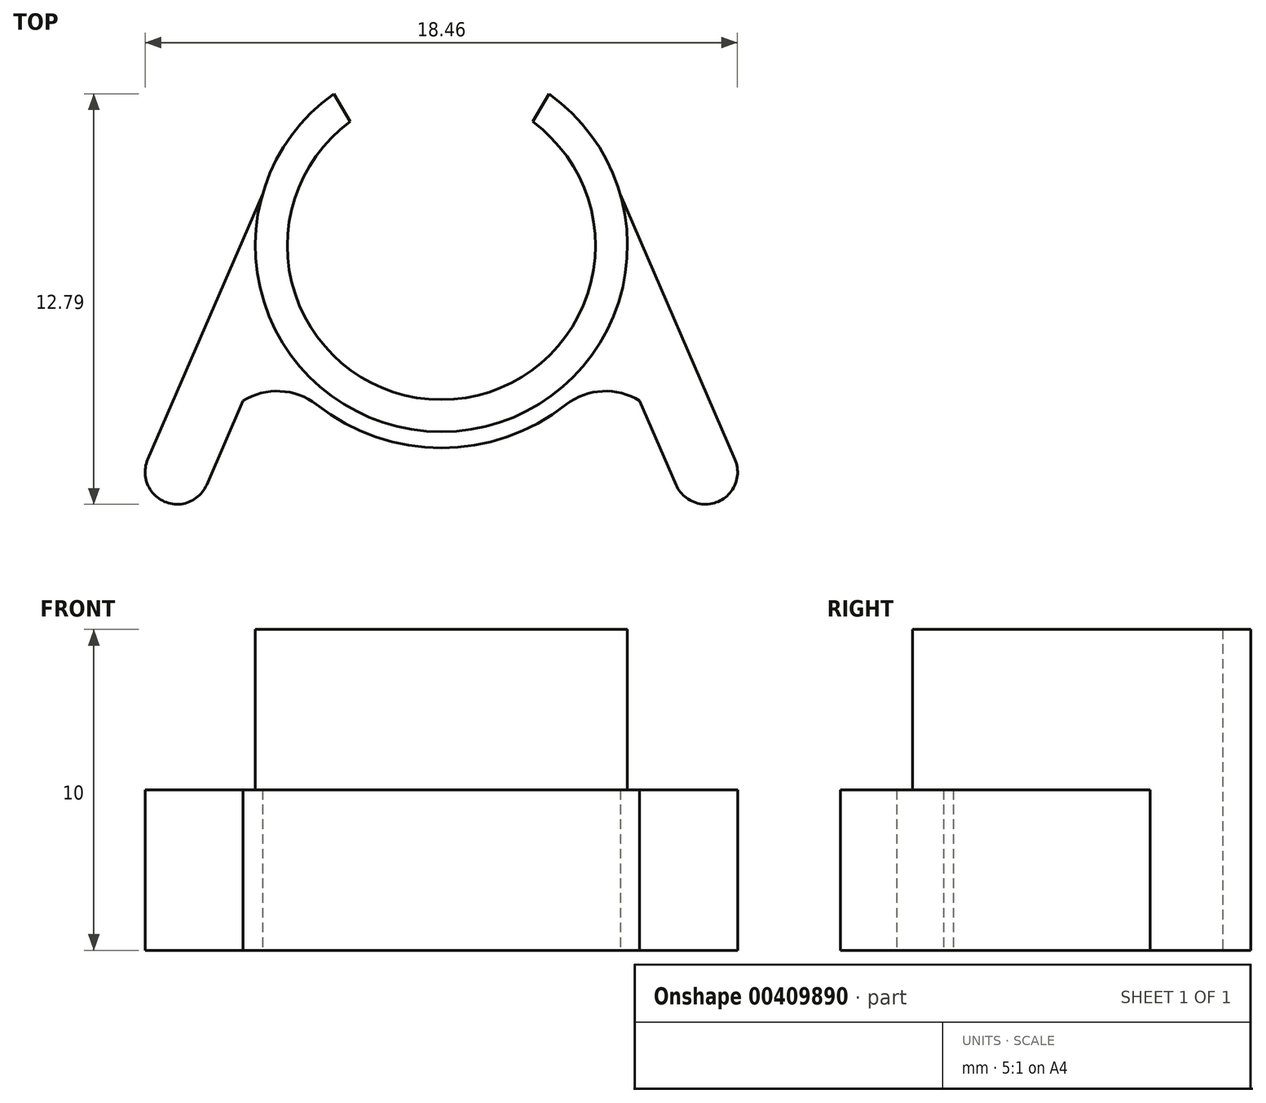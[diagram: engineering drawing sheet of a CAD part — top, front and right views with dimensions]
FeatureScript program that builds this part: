
annotation { "Feature Type Name" : "Feature", "Feature Type Description" : "" }
export const myFeature = defineFeature(function(context is Context, id is Id, definition is map)
    precondition{}
    {
        {
            var Q0;
            Q0=qCreatedBy(makeId("Top.planeOp"),FACE);
            var sketch = newSketch(context, id + "F0", { "sketchPlane" : qUnion([Q0])});
            skCircle(sketch, "E0", {"center": v(0, 0) * mm, "radius": 4.8 * mm});
            skCircle(sketch, "E1", {"center": v(0, 0) * mm, "radius": 5.8 * mm});
            skSolve(sketch);
        }
        {
            var Q0;
            Q0=qSketchRegion(id+"F0",true);
            extrude(context, id + "F1", {"entities" : qUnion([Q0]), "depth" : 10 * mm});
        }
        {
            var Q0;
            Q0=qCreatedBy(makeId("Top.planeOp"),FACE);
            var sketch = newSketch(context, id + "F2", { "sketchPlane" : qUnion([Q0])});
            skArc(sketch, "E2", {"start": v(0, -5.8) * mm, "mid": v(4.63, -3.5) * mm, "end": v(5.58, 1.6) * mm});
            skLineSegment(sketch, "E3", {"start": v(5.58, 1.6) * mm, "end": v(9.15, -6.66) * mm});
            skLineSegment(sketch, "E4", {"start": v(9.15, -6.66) * mm, "end": v(7.31, -7.46) * mm});
            skLineSegment(sketch, "E5", {"start": v(7.31, -7.46) * mm, "end": v(5.2, -2.57) * mm});
            skArc(sketch, "E6", {"start": v(0, -6.3) * mm, "mid": v(4.43, -4.48) * mm, "end": v(6.3, -0.07) * mm});
            skArc(sketch, "E7", {"start": v(6.18, -4.84) * mm, "mid": v(5, -4.54) * mm, "end": v(3.88, -4.97) * mm});
            skLineSegment(sketch, "E8", {"start": v(0, -6.3) * mm, "end": v(0, -5.8) * mm});
            skCircle(sketch, "E9", {"center": v(8.23, -7.06) * mm, "radius": 1 * mm});
            skLineSegment(sketch, "E10.MirrorCS", {"start": v(-5.58, 1.6) * mm, "end": v(-9.15, -6.66) * mm});
            skLineSegment(sketch, "E11.MirrorCS", {"start": v(-7.31, -7.46) * mm, "end": v(-5.2, -2.57) * mm});
            skCircle(sketch, "E12.MirrorC", {"center": v(-8.23, -7.06) * mm, "radius": 1 * mm});
            skArc(sketch, "E13.MirrorCS", {"start": v(-6.18, -4.84) * mm, "mid": v(-5, -4.54) * mm, "end": v(-3.88, -4.97) * mm});
            skArc(sketch, "E14.MirrorCS", {"start": v(0, -6.3) * mm, "mid": v(-4.43, -4.48) * mm, "end": v(-6.3, -0.07) * mm});
            skArc(sketch, "E15.MirrorCS", {"start": v(0, -5.8) * mm, "mid": v(-4.63, -3.5) * mm, "end": v(-5.58, 1.6) * mm});
            skSolve(sketch);
        }
        {
            var Q0;
            Q0=qSketchRegion(id+"F2",true);
            extrude(context, id + "F3", {"entities" : qUnion([Q0]), "operationType" : NewBodyOperationType.ADD, "depth" : 5 * mm});
        }
        {
            var Q0;
            Q0=qCreatedBy(makeId("Top.planeOp"),FACE);
            var sketch = newSketch(context, id + "F4", { "sketchPlane" : qUnion([Q0])});
            skLineSegment(sketch, "E16.bottom", {"start": v(2.8, 0) * mm, "end": v(-2.8, 0) * mm});
            skLineSegment(sketch, "E16.top", {"start": v(2.8, 10) * mm, "end": v(-2.8, 10) * mm});
            skLineSegment(sketch, "E16.left", {"start": v(2.8, 0) * mm, "end": v(2.8, 10) * mm});
            skLineSegment(sketch, "E16.right", {"start": v(-2.8, 0) * mm, "end": v(-2.8, 10) * mm});
            skPoint(sketch, "E16.middle", {"position": v(0, 5) * mm});
            skLineSegment(sketch, "E17", {"start": v(2.8, 10) * mm, "end": v(3.95, 10) * mm});
            skLineSegment(sketch, "E18", {"start": v(3.95, 10) * mm, "end": v(3.95, 5.74) * mm});
            skLineSegment(sketch, "E19", {"start": v(3.95, 5.74) * mm, "end": v(2.8, 3.79) * mm});
            skLineSegment(sketch, "E20.MirrorCS", {"start": v(-2.8, 10) * mm, "end": v(-3.95, 10) * mm});
            skLineSegment(sketch, "E21.MirrorCS", {"start": v(-3.95, 10) * mm, "end": v(-3.95, 5.74) * mm});
            skLineSegment(sketch, "E22.MirrorCS", {"start": v(-3.95, 5.74) * mm, "end": v(-2.8, 3.79) * mm});
            skSolve(sketch);
        }
        {
            var Q0;
            Q0=qSketchRegion(id+"F4",true);
            extrude(context, id + "F5", {"entities" : qUnion([Q0]), "operationType" : NewBodyOperationType.REMOVE, "endBound" : BoundingType.SYMMETRIC, "oppositeDirection" : true, "depth" : 25 * mm});
        }
    });
